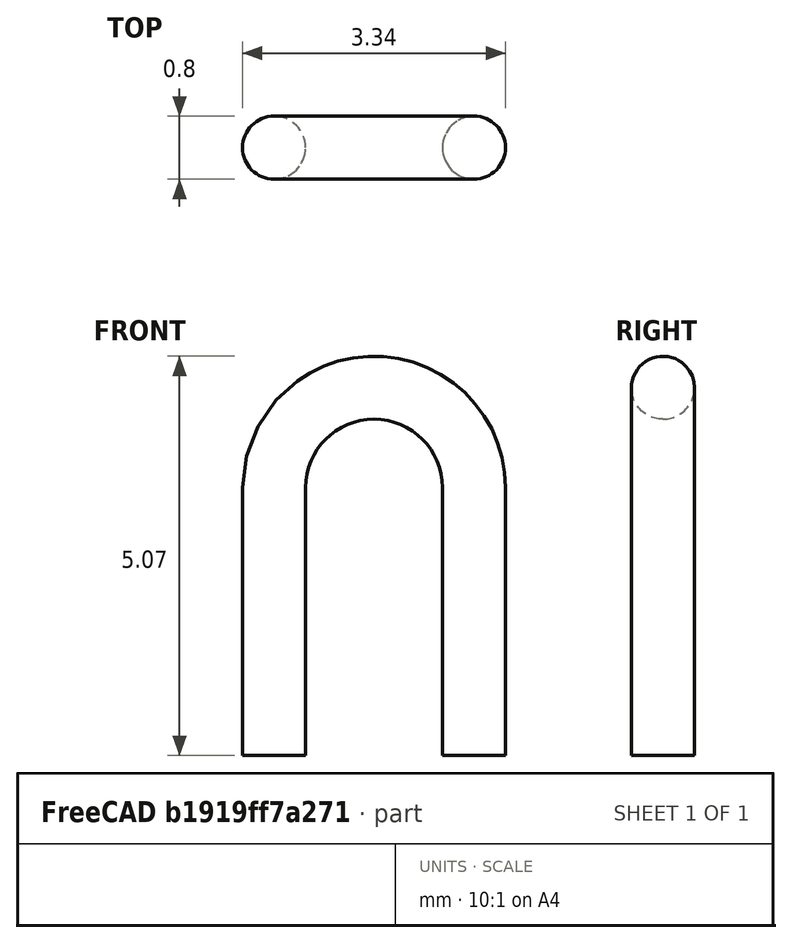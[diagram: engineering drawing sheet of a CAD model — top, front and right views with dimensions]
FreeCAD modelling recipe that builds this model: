
FCSTD DOCUMENT  (FreeCAD 0.17R12018 (Git))
Label: Test_Point_Bridge_Pitch2.54mm_Drill1.0mm
License: All rights reserved
LicenseURL: http://en.wikipedia.org/wiki/All_rights_reserved
objects: Sketcher::SketchObject×2, Spreadsheet::Sheet×1, PartDesign::SubtractivePipe×1, PartDesign::Body×1
note: 5 computed .brp shape members not serialized (recipe doc carries the construction recipe); baked Part::Feature solids carry a one-line shape summary decoded from their .brp

FEATURE [Sketcher::SketchObject] Sketch
  MapMode = 5
  Placement = pos=(0,0,-3) rot=(0,0,1;0rad)
  Support = -> [XY_Plane]
  superPlacement = pos=(0,0,-3) rot=(0,0,1;0rad)
  expr: Constraints[1] = dims.DWire / 2
  sketch-geometry (1):
    g0: Circle CenterX=0 CenterY=0 CenterZ=0 NormalX=0 NormalY=0 NormalZ=1 Radius=0.4
  constraints (2):
    c: Coincident(g0,g-1)
    c: Radius(g0) = 0.4
FEATURE [Spreadsheet::Sheet] Spreadsheet  label="dims"
  cells = A1="DWire"; B1(DWire)=0.80000000000000004; A2="Pitch"; B2(Pitch)=2.54
FEATURE [Sketcher::SketchObject] Sketch001
  MapMode = 5
  Placement = pos=(0,0,0) rot=(1,0,0;1.5708rad)
  Support = -> [XZ_Plane]
  expr: Constraints[10] = dims.DWire / 2
  expr: Constraints[3] = dims.Pitch
  sketch-geometry (4):
    g0: LineSegment StartX=0 StartY=-3 StartZ=0 EndX=0 EndY=0.4 EndZ=0
    g1: LineSegment StartX=2.54 StartY=0.4 StartZ=0 EndX=2.54 EndY=-3 EndZ=0
    g2: LineSegment [constr] StartX=0 StartY=0.4 StartZ=0 EndX=2.54 EndY=0.4 EndZ=0
    g3: ArcOfCircle CenterX=1.27 CenterY=0.4 CenterZ=0 NormalX=0 NormalY=0 NormalZ=1 Radius=1.27 StartAngle=0 EndAngle=3.14159
  constraints (13):
    c: PointOnObject(g0,g-2)
    c: Vertical(g0)
    c: Vertical(g1)
    c: DistanceX(g0,g1) = 2.54
    c: Coincident(g2,g0)
    c: Coincident(g2,g1)
    c: Horizontal(g2)
    c: PointOnObject(g3,g2)
    c: Coincident(g3,g0)
    c: Coincident(g3,g1)
    c: DistanceY(g-1,g3) = 0.4
    c: DistanceY(g0,g-1) = 3
    c: Equal(g1,g0)
FEATURE [PartDesign::SubtractivePipe] SubtractivePipe
  AuxilleryCurvelinear = true
  AuxillerySpineTangent = false
  Binormal = (0,0,0)
  Mode = 0
  Profile = -> Sketch
  Spine = -> Sketch001
  SpineTangent = false
  Transformation = 0
  Transition = 0
FEATURE [PartDesign::Body] Body  label="Test_Point_Bridge_Pitch2.54mm_Drill1.0mm"
  Group = -> [Sketch,Sketch001,SubtractivePipe]
  Origin = -> Origin
  Tip = -> SubtractivePipe
